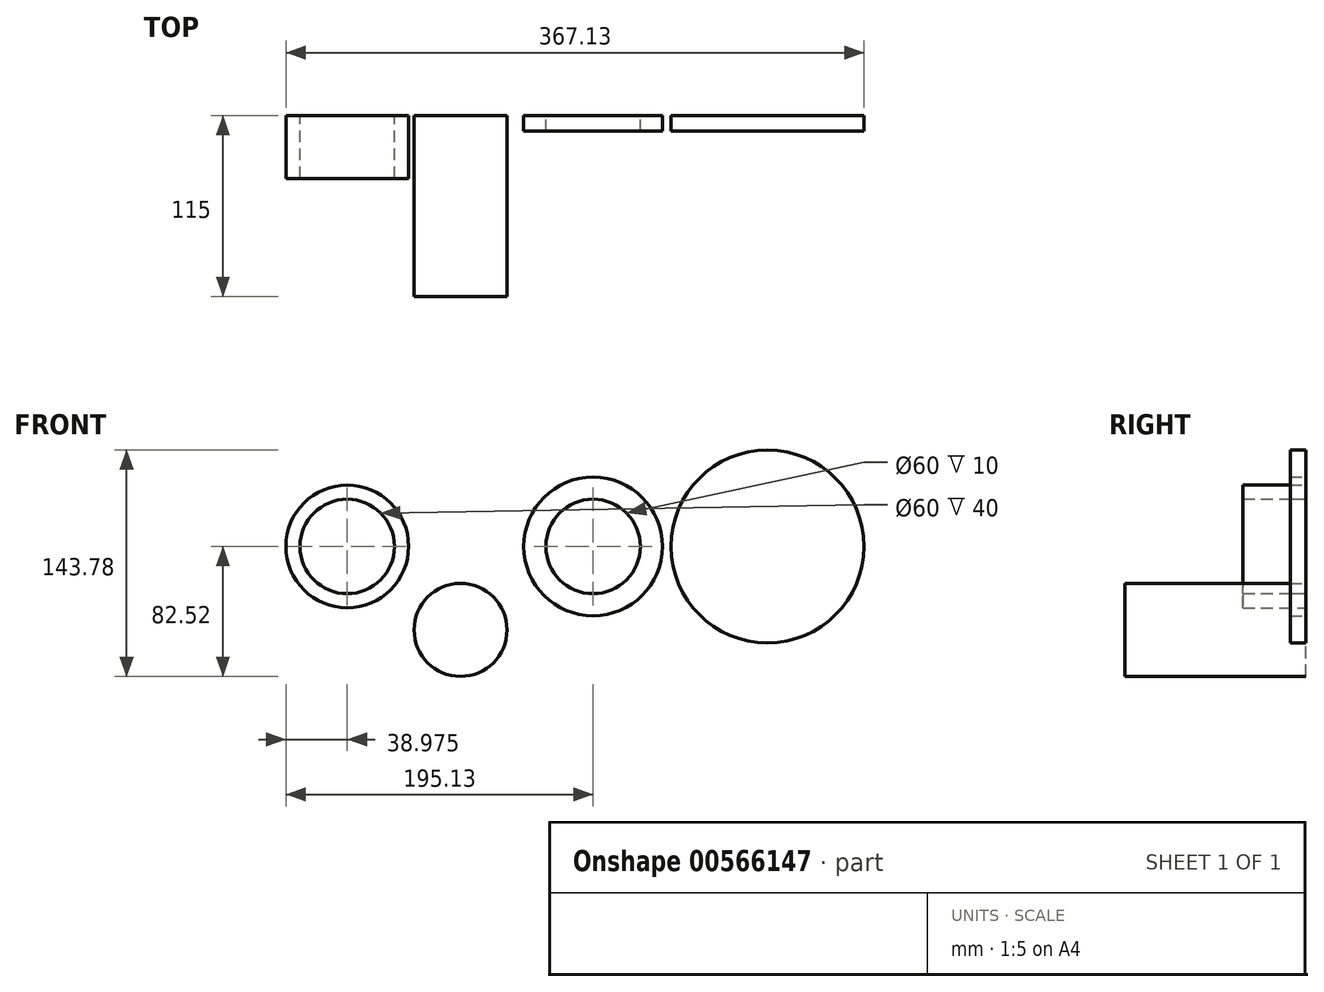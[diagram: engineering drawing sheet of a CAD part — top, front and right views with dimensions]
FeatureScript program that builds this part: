
annotation { "Feature Type Name" : "Feature", "Feature Type Description" : "" }
export const myFeature = defineFeature(function(context is Context, id is Id, definition is map)
    precondition{}
    {
        {
            var Q0;
            Q0=qCreatedBy(makeId("Front.planeOp"),FACE);
            var sketch = newSketch(context, id + "F0", { "sketchPlane" : qUnion([Q0])});
            skCircle(sketch, "E0", {"center": v(-53.44, 0) * mm, "radius": 38.97 * mm});
            skCircle(sketch, "E1", {"center": v(-53.44, 0) * mm, "radius": 30 * mm});
            skSolve(sketch);
        }
        {
            var Q0;
            Q0=qCreatedBy(makeId("Front.planeOp"),FACE);
            var sketch = newSketch(context, id + "F1", { "sketchPlane" : qUnion([Q0])});
            skLineSegment(sketch, "E2", {"start": v(10.86, 0) * mm, "end": v(10.86, 30) * mm});
            skLineSegment(sketch, "E3", {"start": v(10.86, 30) * mm, "end": v(35, 30) * mm});
            skLineSegment(sketch, "E4", {"start": v(35, 30) * mm, "end": v(35, 0) * mm});
            skLineSegment(sketch, "E5", {"start": v(35, 0) * mm, "end": v(10.86, 0) * mm});
            skSolve(sketch);
        }
        {
            var Q0;
            Q0 = qSketchRegion(id + "F1", true);
            var Q1;
            Q1=sQuery(id+"F1.wireOp",EDGE,"E5");
            revolve(context, id + "F2", {"entities" : qUnion([Q0]), "axis" : qUnion([Q1]), "revolveType" : RevolveType.FULL});
        }
        {
            var Q0;
            Q0 = qSketchRegion(id + "F0", true);
            extrude(context, id + "F3", {"entities" : qUnion([Q0]), "depth" : 40 * mm, "offsetDistance" : 25 * mm});
        }
        {
            var Q0;
            Q0=qCreatedBy(makeId("Front.planeOp"),FACE);
            var sketch = newSketch(context, id + "F4", { "sketchPlane" : qUnion([Q0])});
            skCircle(sketch, "E6", {"center": v(102.72, 0) * mm, "radius": 44.07 * mm});
            skCircle(sketch, "E7", {"center": v(102.72, 0) * mm, "radius": 30 * mm});
            skSolve(sketch);
        }
        {
            var Q0;
            Q0 = qSketchRegion(id + "F4", true);
            extrude(context, id + "F5", {"entities" : qUnion([Q0]), "depth" : 10 * mm, "offsetDistance" : 25 * mm});
        }
        {
            var Q0;
            Q0=qCreatedBy(makeId("Front.planeOp"),FACE);
            var sketch = newSketch(context, id + "F6", { "sketchPlane" : qUnion([Q0])});
            skCircle(sketch, "E8", {"center": v(213.46, 0) * mm, "radius": 61.26 * mm});
            skSolve(sketch);
        }
        {
            var Q0;
            Q0 = qSketchRegion(id + "F6", true);
            extrude(context, id + "F7", {"entities" : qUnion([Q0]), "depth" : 10 * mm, "offsetDistance" : 25 * mm});
        }
        {
            var Q0;
            Q0=makeQuery(id+"F2.opRevolve","SWEPT_BODY",BODY,{"disambiguationData":[OSD([sQuery(id+"F1.wireOp",EDGE,"E2"),sQuery(id+"F1.wireOp",EDGE,"E3"),sQuery(id+"F1.wireOp",EDGE,"E4"),sQuery(id+"F1.wireOp",EDGE,"E5")])]});
            deleteBodies(context, id + "F8", {"entities" : qUnion([Q0])});
        }
        {
            var Q0;
            Q0=qCreatedBy(makeId("Front.planeOp"),FACE);
            var sketch = newSketch(context, id + "F9", { "sketchPlane" : qUnion([Q0])});
            skCircle(sketch, "E9", {"center": v(18.5, -53.02) * mm, "radius": 29.5 * mm});
            skSolve(sketch);
        }
        {
            var Q0;
            Q0 = qSketchRegion(id + "F9", true);
            extrude(context, id + "F10", {"entities" : qUnion([Q0]), "depth" : 50 * mm, "offsetDistance" : 25 * mm});
        }
        {
            var Q0;
            Q0=makeQuery(id+"F10.opExtrude","CAP_FACE",FACE,{"disambiguationData":[OSD([sQuery(id+"F9.wireOp",EDGE,"E9")])],"isStart":false});
            extrude(context, id + "F11", {"entities" : qUnion([Q0]), "operationType" : NewBodyOperationType.ADD, "depth" : 25 * mm, "offsetDistance" : 25 * mm});
        }
        {
            var Q0;
            Q0=makeQuery(id+"F11.opExtrude","CAP_FACE",FACE,{"disambiguationData":[OSD([sQuery(id+"F9.wireOp",EDGE,"E9")])],"isStart":false});
            var sketch = newSketch(context, id + "F12", { "sketchPlane" : qUnion([Q0])});
            skSolve(sketch);
        }
        {
            var Q0;
            Q0=makeQuery(id+"F12.imprint","IMPRINT",FACE,{"disambiguationData":[TD([[makeQuery(id+"F12.imprint","IMPRINT",EDGE,{"derivedFrom":makeQuery(id+"F11.opExtrude","CAP_EDGE",EDGE,{"disambiguationData":[OSD([sQuery(id+"F9.wireOp",EDGE,"E9")])],"isStart":false})}),1.0]])]});
            extrude(context, id + "F13", {"entities" : qUnion([Q0]), "operationType" : NewBodyOperationType.ADD, "depth" : 40 * mm, "offsetDistance" : 25 * mm});
        }
    });
